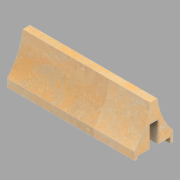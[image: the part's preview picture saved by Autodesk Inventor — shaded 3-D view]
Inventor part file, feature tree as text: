
AUTODESK INVENTOR PART (.ipt)
format: ipt  version: 2022.2 (Build 262287010, 287A)  size: 153,600 bytes
history: native  units: in
note: dims shown in document units (in); Inventor stores cm internally (conversion verified against a paired STEP export)
features: revolve x2, other x1, direct_edit x1
ambient origin geometry x8: Origin, YZ Plane, XZ Plane, XY Plane, X Axis, Y Axis, Z Axis, Center Point
bodies: Solid1 (feature_tree)
feature tree (4):
  other  "Mull (3)"
  direct_edit  "Direct Edit1"
  revolve  "Rotate1"  Angle=90.0deg
  revolve  "Rotate2"  Angle=180.0deg
